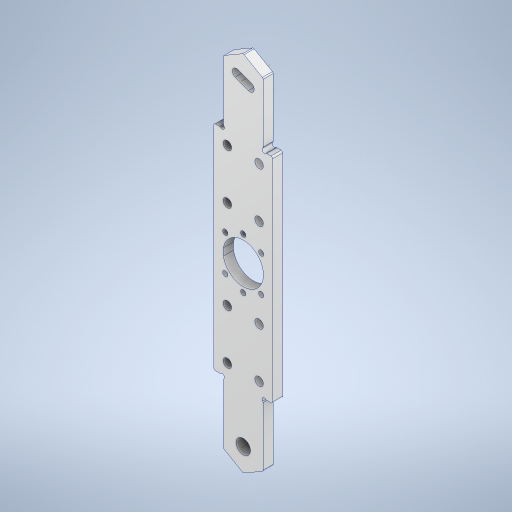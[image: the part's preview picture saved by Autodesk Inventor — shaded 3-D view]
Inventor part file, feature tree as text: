
AUTODESK INVENTOR PART (.ipt)
format: ipt  version: 2024 (Build 280153000, 153)  size: 409,600 bytes
history: native  units: mm
features: sketch x4, extrude x2, mirror x2, hole x2, other x2, projected_geometry x2, fillet x1
ambient origin geometry x8: Origin, YZ Plane, XZ Plane, XY Plane, X Axis, Y Axis, Z Axis, Center Point
bodies: Solid1 (feature_tree)
feature tree (15):
  extrude  "Extrusion1"  Depth=25.0mm
  extrude  "Extrusion2"  Depth=5.3mm
  mirror  "Mirror1"
  mirror  "Mirror2"
  hole  "Hole1"  [1 undecoded]
  hole  "Hole2"  [1 undecoded]
  fillet  "Fillet3"  Radius=6.35mm
  other  "Work Axis1"
  other  "Work Axis2"
  sketch  "Sketch1"  dims[d0=25.0mm d1=268.0mm]
  sketch  "Sketch2"  dims[d2=200.0mm d3=5.3mm]
  projected_geometry  "Projected Loop1"
  sketch  "Sketch3"  dims[d4=9.0mm d5=9.0mm]
  projected_geometry  "Projected Loop2"
  sketch  "Sketch4"  dims[d12=134.75mm d13=37.0mm d14=6.35mm d15=0.0mm d16=0.75mm d17=2.75mm d18=0.75mm d19=0.0mm d20=0.0mm d21=32.0mm d22=45.0deg d23=3.242mm d24=8.0mm d25=4.0mm d26=2.0mm d27=90.0deg d28=8.0mm d29=20.594885mm d30=20.0mm d32=8.0mm d33=5.3mm d34=8.0mm d35=4.0mm d36=2.0mm d37=90.0deg d38=8.0mm d39=20.594885mm d42=1.0mm d43=25.4mm d44=56.0mm]
note: 2 required parameter values undecoded (feature->parameter linkage not recoverable at this tier; creation-order binding heuristic only, values carry confidence <= 0.55)
